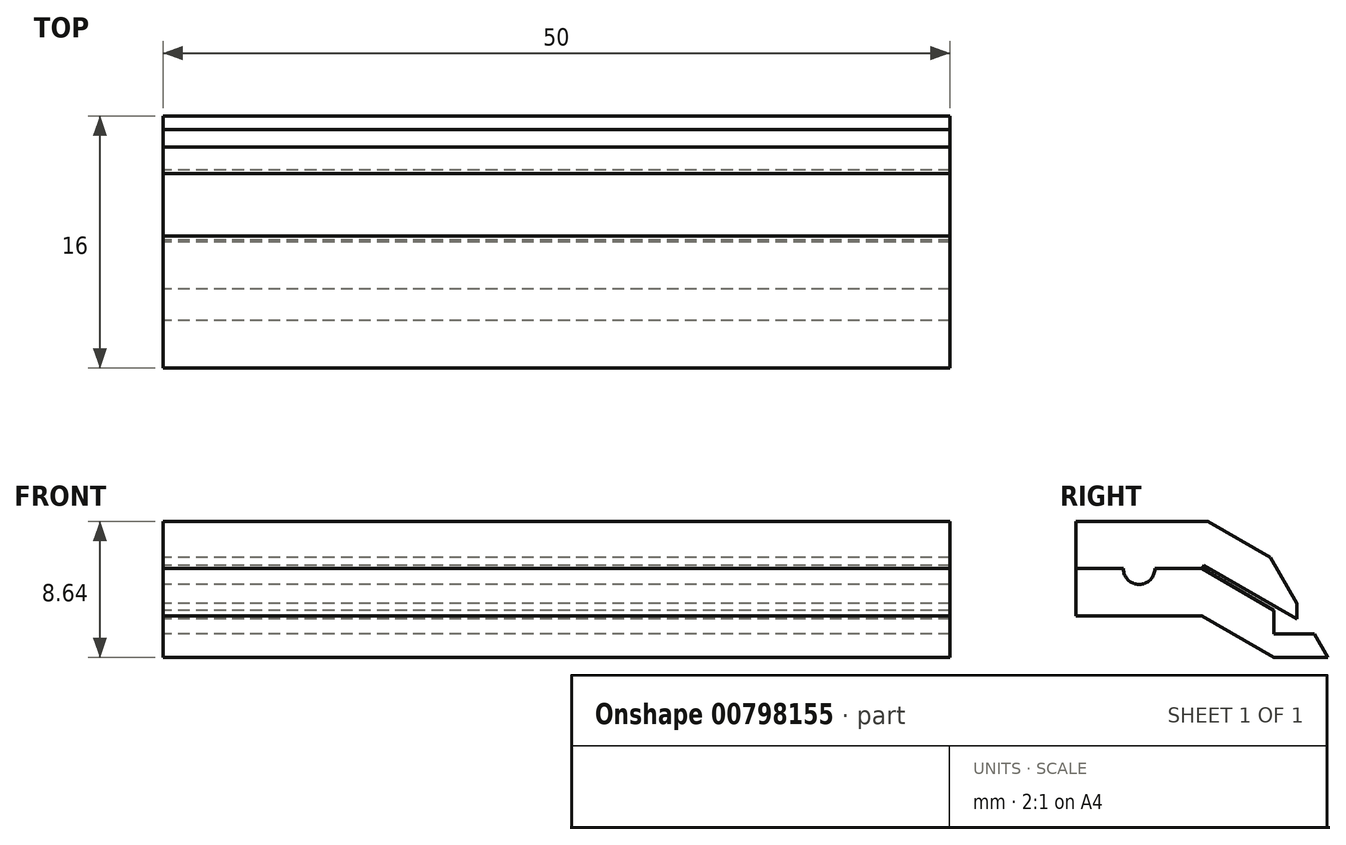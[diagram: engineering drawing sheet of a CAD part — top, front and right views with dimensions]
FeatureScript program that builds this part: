
annotation { "Feature Type Name" : "Feature", "Feature Type Description" : "" }
export const myFeature = defineFeature(function(context is Context, id is Id, definition is map)
    precondition{}
    {
        {
            var Q0;
            Q0=qCreatedBy(makeId("Right.planeOp"),FACE);
            var sketch = newSketch(context, id + "F0", { "sketchPlane" : qUnion([Q0])});
            skLineSegment(sketch, "E0.top", {"start": v(0, 6) * mm, "end": v(8.37, 6) * mm});
            skLineSegment(sketch, "E1", {"start": v(14.02, -0.18) * mm, "end": v(8.13, 3.22) * mm});
            skLineSegment(sketch, "E2", {"start": v(8.13, 3.22) * mm, "end": v(8, 3) * mm});
            skLineSegment(sketch, "E3", {"start": v(8, 3) * mm, "end": v(12.57, 0.36) * mm});
            skLineSegment(sketch, "E4", {"start": v(12.57, 0.36) * mm, "end": v(12.57, -1.14) * mm});
            skLineSegment(sketch, "E5", {"start": v(12.57, -1.14) * mm, "end": v(15.14, -1.14) * mm});
            skLineSegment(sketch, "E6", {"start": v(15.14, -1.14) * mm, "end": v(16, -2.64) * mm});
            skLineSegment(sketch, "E7", {"start": v(16, -2.64) * mm, "end": v(12.57, -2.64) * mm});
            skLineSegment(sketch, "E8", {"start": v(8, 3) * mm, "end": v(5, 3) * mm});
            skLineSegment(sketch, "E9", {"start": v(8.06, 3.1) * mm, "end": v(15, -0.9) * mm, "construction": true});
            skLineSegment(sketch, "E10", {"start": v(0, 0) * mm, "end": v(0, 6) * mm});
            skLineSegment(sketch, "E11", {"start": v(14.02, 0.8) * mm, "end": v(15.14, -1.14) * mm, "construction": true});
            skLineSegment(sketch, "E12", {"start": v(15, -0.9) * mm, "end": v(15, -1.14) * mm, "construction": true});
            skLineSegment(sketch, "E13", {"start": v(14.93, -1) * mm, "end": v(15.06, -0.78) * mm, "construction": true});
            skLineSegment(sketch, "E14", {"start": v(15.06, -0.78) * mm, "end": v(14.02, -0.18) * mm, "construction": true});
            skLineSegment(sketch, "E15", {"start": v(14.02, -0.18) * mm, "end": v(14.02, 0.8) * mm});
            skLineSegment(sketch, "E16", {"start": v(14.02, 0.8) * mm, "end": v(12.34, 3.7) * mm});
            skLineSegment(sketch, "E17", {"start": v(8, 0) * mm, "end": v(12.57, -2.64) * mm});
            skLineSegment(sketch, "E18", {"start": v(8, 0) * mm, "end": v(0, 0) * mm});
            skLineSegment(sketch, "E19", {"start": v(12.57, -1.14) * mm, "end": v(12.57, -2.64) * mm, "construction": true});
            skLineSegment(sketch, "E20", {"start": v(11.07, 1.52) * mm, "end": v(12.34, 3.7) * mm, "construction": true});
            skLineSegment(sketch, "E21", {"start": v(12.34, 3.7) * mm, "end": v(8.37, 6) * mm});
            skLineSegment(sketch, "E22", {"start": v(4, 0) * mm, "end": v(4, 2) * mm, "construction": true});
            skArc(sketch, "E23", {"start": v(3, 3) * mm, "mid": v(4, 2) * mm, "end": v(5, 3) * mm});
            skLineSegment(sketch, "E24.trimOffspring", {"start": v(3, 3) * mm, "end": v(0, 3) * mm});
            skSolve(sketch);
        }
        {
            var Q0;
            {var subQ1=sQuery(id+"F0.wireOp",EDGE,"E0.top");Q0=makeQuery(id+"F0.imprint","IMPRINT",FACE,{"disambiguationData":[TD([[makeQuery(id+"F0.imprint","IMPRINT",EDGE,{"derivedFrom":subQ1}),-1.0]])]});}
            extrude(context, id + "F1", {"entities" : qUnion([Q0]), "endBound" : BoundingType.SYMMETRIC, "depth" : 50 * mm, "offsetDistance" : 25 * mm});
        }
        {
            var Q0;
            Q0=makeQuery(id+"F0.imprint","IMPRINT",FACE,{"disambiguationData":[TD([[makeQuery(id+"F0.imprint","IMPRINT",EDGE,{"derivedFrom":sQuery(id+"F0.wireOp",EDGE,"E3")}),-1.0]])]});
            extrude(context, id + "F2", {"entities" : qUnion([Q0]), "endBound" : BoundingType.SYMMETRIC, "depth" : 50 * mm, "offsetDistance" : 25 * mm});
        }
    });
